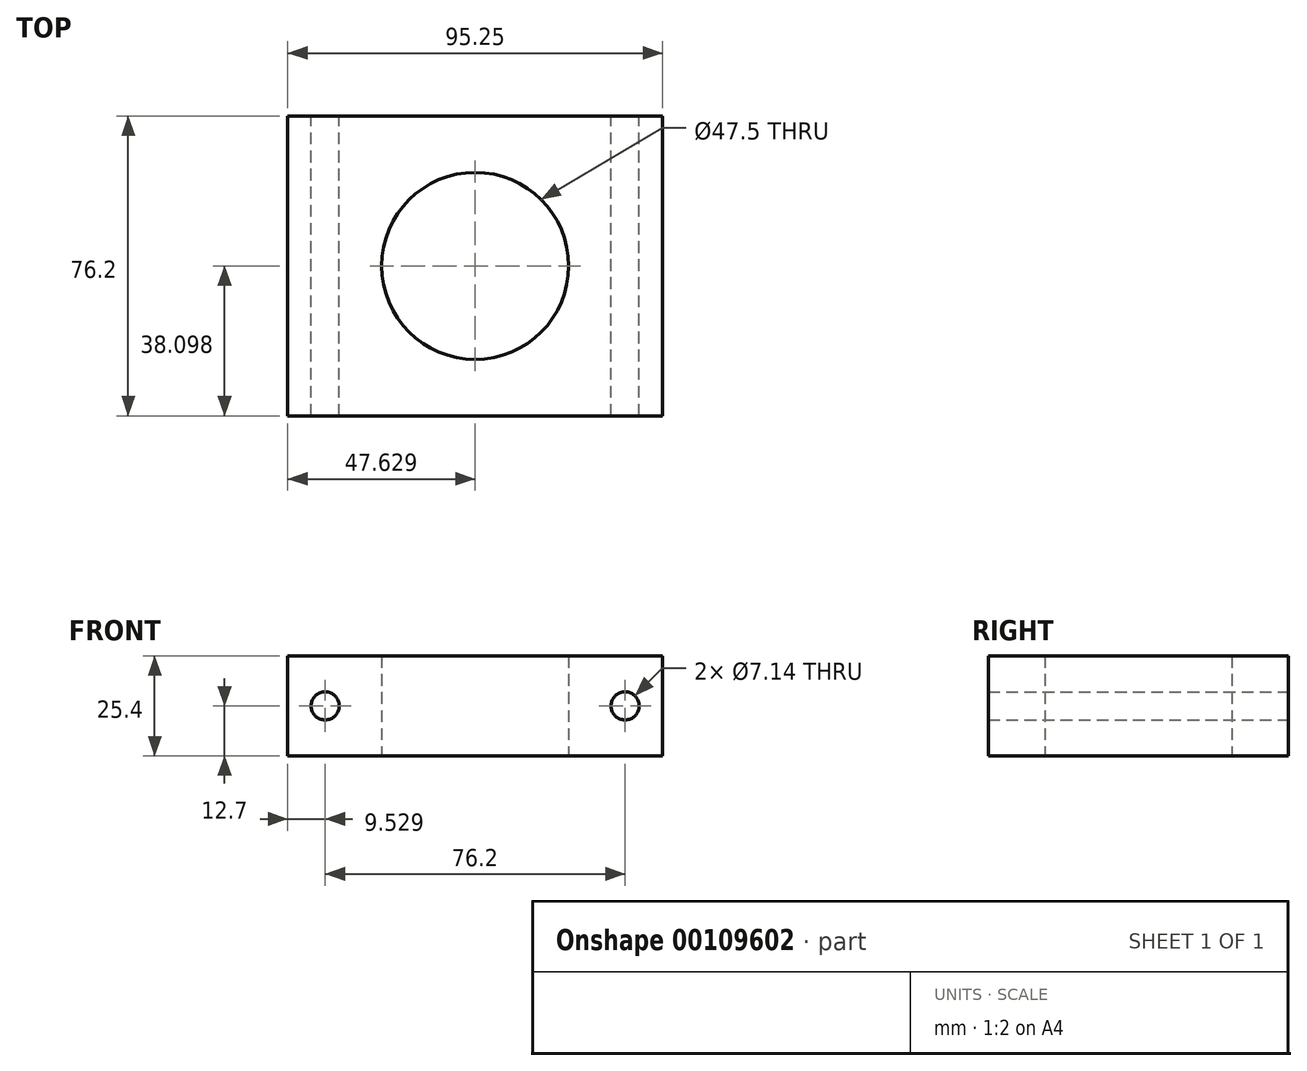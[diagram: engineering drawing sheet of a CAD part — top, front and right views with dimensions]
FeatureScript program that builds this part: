
annotation { "Feature Type Name" : "Feature", "Feature Type Description" : "" }
export const myFeature = defineFeature(function(context is Context, id is Id, definition is map)
    precondition{}
    {
        {
            var Q0;
            Q0=qCreatedBy(makeId("Top.planeOp"),FACE);
            var sketch = newSketch(context, id + "F0", { "sketchPlane" : qUnion([Q0])});
            skLineSegment(sketch, "E0.bottom", {"start": v(-45.08, 32.77) * mm, "end": v(50.17, 32.77) * mm});
            skLineSegment(sketch, "E0.top", {"start": v(-45.08, -43.43) * mm, "end": v(50.17, -43.43) * mm});
            skLineSegment(sketch, "E0.left", {"start": v(-45.08, 32.77) * mm, "end": v(-45.08, -43.43) * mm});
            skLineSegment(sketch, "E0.right", {"start": v(50.17, 32.77) * mm, "end": v(50.17, -43.43) * mm});
            skCircle(sketch, "E1", {"center": v(2.55, -5.33) * mm, "radius": 23.75 * mm});
            skPoint(sketch, "E1.centerSnap0", {"position": v(-45.08, -5.33) * mm});
            skPoint(sketch, "E1.centerSnap1", {"position": v(2.55, -43.43) * mm});
            skSolve(sketch);
        }
        {
            var Q0;
            Q0=makeQuery(id+"F0.imprint","IMPRINT",FACE,{"disambiguationData":[TD([[makeQuery(id+"F0.imprint","IMPRINT",EDGE,{"derivedFrom":sQuery(id+"F0.wireOp",EDGE,"E0.bottom")}),-1.0]])]});
            extrude(context, id + "F1", {"entities" : qUnion([Q0]), "depth" : 25.4 * mm});
        }
        {
            var Q0;
            Q0=makeQuery(id+"F1.opExtrude","SWEPT_FACE",FACE,{"disambiguationData":[OSD([sQuery(id+"F0.wireOp",EDGE,"E0.bottom")])]});
            var sketch = newSketch(context, id + "F2", { "sketchPlane" : qUnion([Q0])});
            skLineSegment(sketch, "E2", {"start": v(-50.17, 12.7) * mm, "end": v(45.08, 12.7) * mm, "construction": true});
            skLineSegment(sketch, "E3", {"start": v(-2.55, 0) * mm, "end": v(-2.55, 25.4) * mm, "construction": true});
            skCircle(sketch, "E4", {"center": v(-40.65, 12.7) * mm, "radius": 3.57 * mm});
            skCircle(sketch, "E5", {"center": v(35.55, 12.7) * mm, "radius": 3.57 * mm});
            skSolve(sketch);
        }
        {
            var Q0;
            Q0=makeQuery(id+"F2.imprint","IMPRINT",FACE,{"disambiguationData":[TD([[makeQuery(id+"F2.imprint","IMPRINT",EDGE,{"derivedFrom":sQuery(id+"F2.wireOp",EDGE,"E5")}),1.0]])]});
            var Q1;
            Q1=makeQuery(id+"F2.imprint","IMPRINT",FACE,{"disambiguationData":[TD([[makeQuery(id+"F2.imprint","IMPRINT",EDGE,{"derivedFrom":sQuery(id+"F2.wireOp",EDGE,"E4")}),1.0]])]});
            extrude(context, id + "F3", {"entities" : qUnion([Q0, Q1]), "operationType" : NewBodyOperationType.REMOVE, "oppositeDirection" : true, "depth" : 114.62 * mm});
        }
    });
